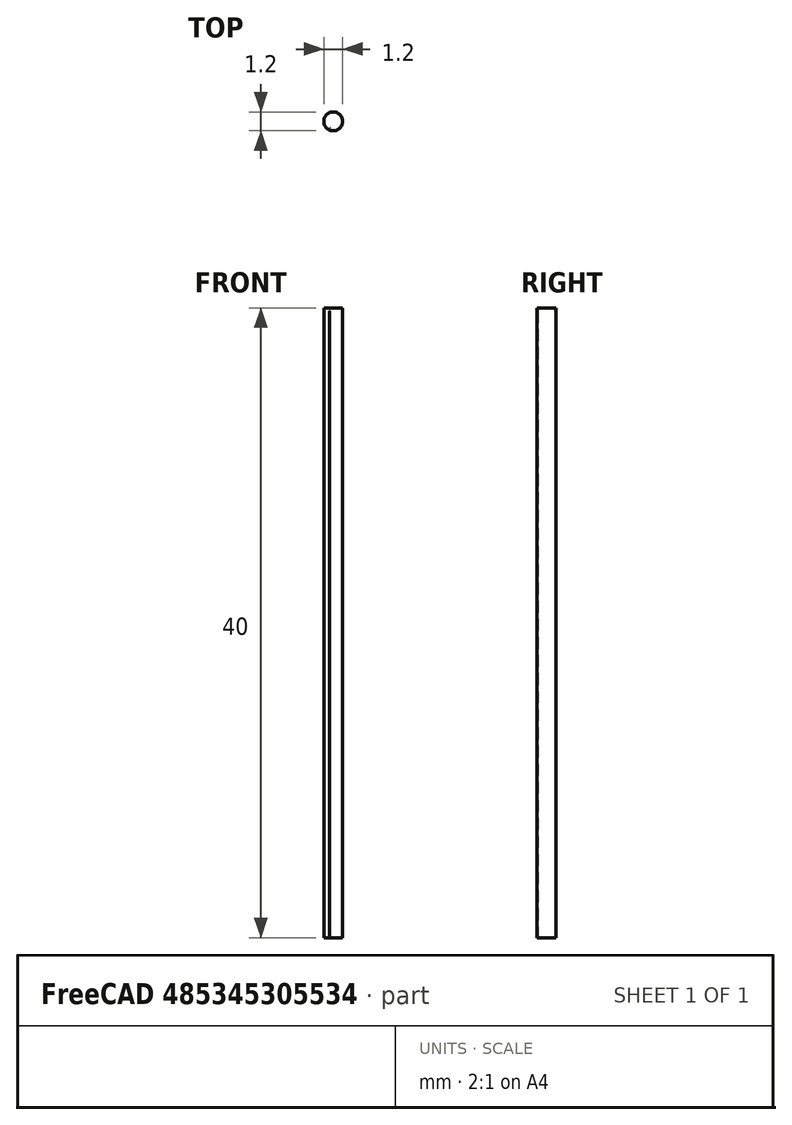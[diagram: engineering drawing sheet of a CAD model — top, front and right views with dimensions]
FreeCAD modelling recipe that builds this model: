
FCSTD DOCUMENT  (FreeCAD 0.16R6712 (Git))
Label: pencil
License: All rights reserved
LicenseURL: http://en.wikipedia.org/wiki/All_rights_reserved
objects: Sketcher::SketchObject×2, PartDesign::Pad×1, PartDesign::Pocket×1, PartDesign::PolarPattern×1, PartDesign::Fillet×1, Mesh::Feature×1
note: 8 computed .brp shape members not serialized (recipe doc carries the construction recipe); baked Part::Feature solids carry a one-line shape summary decoded from their .brp

FEATURE [Sketcher::SketchObject] Sketch
  sketch-geometry (1):
    g0: Circle CenterX=0 CenterY=0 CenterZ=0 NormalX=0 NormalY=0 NormalZ=1 Radius=0.6
  constraints (2):
    c: Radius(g0) = 0.6
    c: Coincident(g0,g-1)
FEATURE [PartDesign::Pad] Pad
  Length = 20
  Length2 = 20
  Sketch = -> Sketch
  Type = 4
FEATURE [Sketcher::SketchObject] Sketch001
  Placement = pos=(0,0,20) rot=(0,0,1;0rad)
  Support = -> Pad [Face3]
  sketch-geometry (4):
    g0: LineSegment StartX=-0.3 StartY=0.85 StartZ=0 EndX=0.3 EndY=0.85 EndZ=0
    g1: LineSegment StartX=0.3 StartY=0.85 StartZ=0 EndX=0.3 EndY=0.55 EndZ=0
    g2: LineSegment StartX=0.3 StartY=0.55 StartZ=0 EndX=-0.3 EndY=0.55 EndZ=0
    g3: LineSegment StartX=-0.3 StartY=0.55 StartZ=0 EndX=-0.3 EndY=0.85 EndZ=0
  constraints (12):
    c: Coincident(g0,g1)
    c: Coincident(g1,g2)
    c: Coincident(g2,g3)
    c: Coincident(g3,g0)
    c: Horizontal(g0)
    c: Horizontal(g2)
    c: Vertical(g1)
    c: Vertical(g3)
    c: DistanceY(g-1,g1) = 0.55
    c: Symmetric(g0,g0,g-2)
    c: Distance(g0,g2) = 0.3
    c: DistanceX(g-2,g0) = 0.3
FEATURE [PartDesign::Pocket] Pocket
  Length = 50
  Sketch = -> Sketch001
  Type = 0
FEATURE [PartDesign::PolarPattern] PolarPattern
  Angle = 360
  Axis = -> Sketch001 [N_Axis]
  Occurrences = 6
  Originals = -> [Pocket]
FEATURE [PartDesign::Fillet] Fillet
  Base = -> PolarPattern [Edge33,Edge32,Edge34,Edge35,Edge36,Edge31,Edge18,Edge2,Edge30,Edge39,Edge38,Edge3,Edge17,Edge19,Edge20,Edge21,Edge22,Edge23,Edge24,Edge25,Edge26,Edge27,Edge28,Edge29]
  Radius = 0.2
FEATURE [Mesh::Feature] Mesh  label="Fillet (Meshed)"
